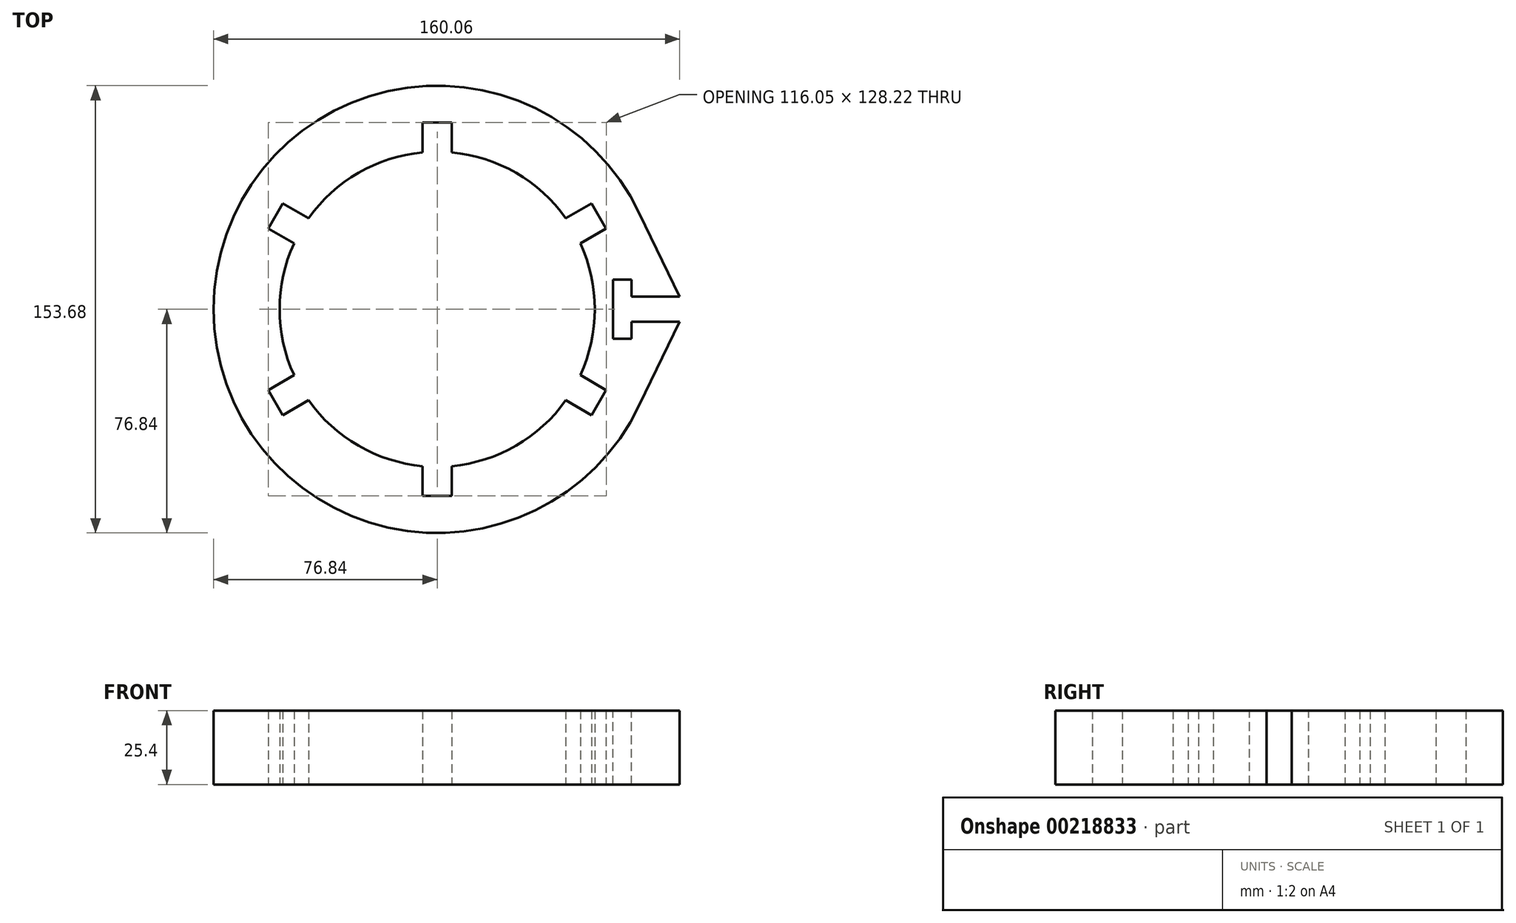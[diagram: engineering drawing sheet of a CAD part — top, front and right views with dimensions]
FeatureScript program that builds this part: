
annotation { "Feature Type Name" : "Feature", "Feature Type Description" : "" }
export const myFeature = defineFeature(function(context is Context, id is Id, definition is map)
    precondition{}
    {
        {
            var Q0;
            Q0=qCreatedBy(makeId("Top.planeOp"),FACE);
            var sketch = newSketch(context, id + "F0", { "sketchPlane" : qUnion([Q0])});
            skCircle(sketch, "E0", {"center": v(0, 0) * mm, "radius": 54.11 * mm});
            skLineSegment(sketch, "E1.bottom", {"start": v(5, 64.11) * mm, "end": v(-5, 64.11) * mm});
            skLineSegment(sketch, "E1.top", {"start": v(5, 44.11) * mm, "end": v(-5, 44.11) * mm});
            skLineSegment(sketch, "E1.left", {"start": v(5, 64.11) * mm, "end": v(5, 44.11) * mm});
            skLineSegment(sketch, "E1.right", {"start": v(-5, 64.11) * mm, "end": v(-5, 44.11) * mm});
            skPoint(sketch, "E1.middle", {"position": v(0, 54.11) * mm});
            skLineSegment(sketch, "E2.1.0", {"start": v(-58.02, 27.73) * mm, "end": v(-40.7, 17.73) * mm});
            skLineSegment(sketch, "E2.1.1", {"start": v(-53.02, 36.39) * mm, "end": v(-58.02, 27.73) * mm});
            skLineSegment(sketch, "E2.1.2", {"start": v(-35.7, 26.39) * mm, "end": v(-40.7, 17.73) * mm});
            skLineSegment(sketch, "E2.1.3", {"start": v(-53.02, 36.39) * mm, "end": v(-35.7, 26.39) * mm});
            skLineSegment(sketch, "E2.2.0", {"start": v(-53.02, -36.39) * mm, "end": v(-35.7, -26.39) * mm});
            skLineSegment(sketch, "E2.2.1", {"start": v(-58.02, -27.73) * mm, "end": v(-53.02, -36.39) * mm});
            skLineSegment(sketch, "E2.2.2", {"start": v(-40.7, -17.73) * mm, "end": v(-35.7, -26.39) * mm});
            skLineSegment(sketch, "E2.2.3", {"start": v(-58.02, -27.73) * mm, "end": v(-40.7, -17.73) * mm});
            skLineSegment(sketch, "E2.3.0", {"start": v(5, -64.11) * mm, "end": v(5, -44.11) * mm});
            skLineSegment(sketch, "E2.3.1", {"start": v(-5, -64.11) * mm, "end": v(5, -64.11) * mm});
            skLineSegment(sketch, "E2.3.2", {"start": v(-5, -44.11) * mm, "end": v(5, -44.11) * mm});
            skLineSegment(sketch, "E2.3.3", {"start": v(-5, -64.11) * mm, "end": v(-5, -44.11) * mm});
            skLineSegment(sketch, "E2.4.0", {"start": v(58.02, -27.73) * mm, "end": v(40.7, -17.73) * mm});
            skLineSegment(sketch, "E2.4.1", {"start": v(53.02, -36.39) * mm, "end": v(58.02, -27.73) * mm});
            skLineSegment(sketch, "E2.4.2", {"start": v(35.7, -26.39) * mm, "end": v(40.7, -17.73) * mm});
            skLineSegment(sketch, "E2.4.3", {"start": v(53.02, -36.39) * mm, "end": v(35.7, -26.39) * mm});
            skLineSegment(sketch, "E2.5.0", {"start": v(53.02, 36.39) * mm, "end": v(35.7, 26.39) * mm});
            skLineSegment(sketch, "E2.5.1", {"start": v(58.02, 27.73) * mm, "end": v(53.02, 36.39) * mm});
            skLineSegment(sketch, "E2.5.2", {"start": v(40.7, 17.73) * mm, "end": v(35.7, 26.39) * mm});
            skLineSegment(sketch, "E2.5.3", {"start": v(58.02, 27.73) * mm, "end": v(40.7, 17.73) * mm});
            skLineSegment(sketch, "E2.anchor1", {"start": v(0, 0) * mm, "end": v(5, 44.11) * mm, "construction": true});
            skLineSegment(sketch, "E2.anchor2", {"start": v(0, 0) * mm, "end": v(5, 44.11) * mm, "construction": true});
            skCircle(sketch, "E3", {"center": v(0, 0) * mm, "radius": 76.84 * mm});
            skSolve(sketch);
        }
        {
            var Q0;
            {var subQ19=sQuery(id+"F0.wireOp",EDGE,"E2.1.1");Q0=makeQuery(id+"F0.imprint","IMPRINT",FACE,{"disambiguationData":[TD([[makeQuery(id+"F0.imprint","IMPRINT",EDGE,{"derivedFrom":subQ19}),-1.0]])]});}
            extrude(context, id + "F1", {"entities" : qUnion([Q0]), "depth" : 25.4 * mm});
        }
        {
            var Q0;
            Q0=makeQuery(id+"F1.opExtrude","CAP_FACE",FACE,{"disambiguationData":[OSD([sQuery(id+"F0.wireOp",EDGE,"E0"),sQuery(id+"F0.wireOp",EDGE,"E2.1.0"),sQuery(id+"F0.wireOp",EDGE,"E2.1.1"),sQuery(id+"F0.wireOp",EDGE,"E2.1.3"),sQuery(id+"F0.wireOp",EDGE,"E2.2.0"),sQuery(id+"F0.wireOp",EDGE,"E2.2.1"),sQuery(id+"F0.wireOp",EDGE,"E2.2.3"),sQuery(id+"F0.wireOp",EDGE,"E2.3.0"),sQuery(id+"F0.wireOp",EDGE,"E2.3.1"),sQuery(id+"F0.wireOp",EDGE,"E2.3.3"),sQuery(id+"F0.wireOp",EDGE,"E2.4.0"),sQuery(id+"F0.wireOp",EDGE,"E2.4.1"),sQuery(id+"F0.wireOp",EDGE,"E2.4.3"),sQuery(id+"F0.wireOp",EDGE,"E2.5.0"),sQuery(id+"F0.wireOp",EDGE,"E2.5.1"),sQuery(id+"F0.wireOp",EDGE,"E2.5.3"),sQuery(id+"F0.wireOp",EDGE,"E3"),sQuery(id+"F0.wireOp",EDGE,"E1.bottom"),sQuery(id+"F0.wireOp",EDGE,"E1.right"),sQuery(id+"F0.wireOp",EDGE,"E1.left")])],"isStart":false});
            var sketch = newSketch(context, id + "F2", { "sketchPlane" : qUnion([Q0])});
            skLineSegment(sketch, "E4", {"start": v(76.16, -10.19) * mm, "end": v(71.64, -4.32) * mm});
            skLineSegment(sketch, "E5", {"start": v(71.64, -4.32) * mm, "end": v(66.68, -4.32) * mm});
            skLineSegment(sketch, "E6", {"start": v(66.68, -4.32) * mm, "end": v(66.68, -10.16) * mm});
            skLineSegment(sketch, "E7", {"start": v(66.68, -10.16) * mm, "end": v(60.33, -10.16) * mm});
            skLineSegment(sketch, "E8", {"start": v(60.33, -10.16) * mm, "end": v(60.33, 0) * mm});
            skPoint(sketch, "E8.endSnap0", {"position": v(54.11, 0) * mm});
            skLineSegment(sketch, "E9", {"start": v(54.11, 0) * mm, "end": v(76.84, 0) * mm});
            skLineSegment(sketch, "E10.MirrorCS", {"start": v(60.33, 10.16) * mm, "end": v(60.33, 0) * mm});
            skLineSegment(sketch, "E11.MirrorCS", {"start": v(66.68, 10.16) * mm, "end": v(60.33, 10.16) * mm});
            skLineSegment(sketch, "E12.MirrorCS", {"start": v(66.68, 4.32) * mm, "end": v(66.68, 10.16) * mm});
            skLineSegment(sketch, "E13.MirrorCS", {"start": v(71.64, 4.32) * mm, "end": v(66.68, 4.32) * mm});
            skLineSegment(sketch, "E14.MirrorCS", {"start": v(76.16, 10.19) * mm, "end": v(71.64, 4.32) * mm});
            skLineSegment(sketch, "E15", {"start": v(71.64, -4.32) * mm, "end": v(76.84, -4.32) * mm});
            skLineSegment(sketch, "E16", {"start": v(71.64, 4.32) * mm, "end": v(76.72, 4.32) * mm});
            skFitSpline(sketch, "E17", {"points": [v(69.43, -32.92) * mm, v(79, -10.72) * mm, v(85.43, -6.68) * mm], "startDerivative": vector(14, 42.13) * mm, "endDerivative": vector(18.45, 7.04) * mm});
            skLineSegment(sketch, "E18", {"start": v(85.43, -6.68) * mm, "end": v(83.22, -4.32) * mm});
            skLineSegment(sketch, "E19", {"start": v(83.22, -4.32) * mm, "end": v(76.84, -4.32) * mm});
            skFitSpline(sketch, "E20.MirrorCS", {"points": [v(69.43, 32.92) * mm, v(79, 10.72) * mm, v(85.43, 6.68) * mm], "startDerivative": vector(14, -42.13) * mm, "endDerivative": vector(18.45, -7.04) * mm});
            skLineSegment(sketch, "E21.MirrorCS", {"start": v(83.22, 4.32) * mm, "end": v(76.84, 4.32) * mm});
            skLineSegment(sketch, "E22.MirrorCS", {"start": v(85.43, 6.68) * mm, "end": v(83.22, 4.32) * mm});
            skLineSegment(sketch, "E23", {"start": v(76.16, -10.19) * mm, "end": v(79, -10.72) * mm});
            skLineSegment(sketch, "E24", {"start": v(76.16, 10.19) * mm, "end": v(79, 10.72) * mm});
            skLineSegment(sketch, "E25", {"start": v(79, 10.72) * mm, "end": v(83.22, 4.32) * mm});
            skLineSegment(sketch, "E26", {"start": v(76.16, 10.19) * mm, "end": v(76.72, 4.32) * mm});
            skLineSegment(sketch, "E27", {"start": v(69.43, -32.92) * mm, "end": v(83.22, -4.32) * mm});
            skLineSegment(sketch, "E28", {"start": v(69.43, 32.92) * mm, "end": v(83.22, 4.32) * mm});
            skLineSegment(sketch, "E29", {"start": v(76.84, 4.32) * mm, "end": v(76.72, 4.32) * mm});
            skSolve(sketch);
        }
        {
            var Q0;
            {var subQ0=sQuery(id+"F2.wireOp",EDGE,"E10.MirrorCS");Q0=makeQuery(id+"F2.imprint","IMPRINT",FACE,{"disambiguationData":[TD([[makeQuery(id+"F2.imprint","IMPRINT",EDGE,{"derivedFrom":subQ0}),1.0]])]});}
            var Q1;
            {var subQ1=sQuery(id+"F2.wireOp",EDGE,"E5");Q1=makeQuery(id+"F2.imprint","IMPRINT",FACE,{"disambiguationData":[TD([[makeQuery(id+"F2.imprint","IMPRINT",EDGE,{"derivedFrom":subQ1}),-1.0]])]});}
            extrude(context, id + "F3", {"entities" : qUnion([Q0, Q1]), "operationType" : NewBodyOperationType.REMOVE, "oppositeDirection" : true, "depth" : 2540 * mm});
        }
        {
            var Q0;
            {var subQ0=sQuery(id+"F2.wireOp",EDGE,"E20.MirrorCS");var subQ2=makeQuery(id+"F1.opExtrude","CAP_EDGE",EDGE,{"disambiguationData":[OSD([sQuery(id+"F0.wireOp",EDGE,"E3")])],"isStart":false});var subQ3=makeQuery(id+"F2.imprint","INTERSECT",VERTEX,{"derivedFrom":[subQ2,subQ0]});Q0=makeQuery(id+"F2.imprint","IMPRINT",FACE,{"disambiguationData":[TD([[makeQuery(id+"F2.imprint","IMPRINT",EDGE,{"disambiguationData":[TD([[subQ3,-1.0]])],"derivedFrom":subQ0}),1.0]])]});}
            var Q1;
            {var subQ0=sQuery(id+"F2.wireOp",EDGE,"E24");Q1=makeQuery(id+"F2.imprint","IMPRINT",FACE,{"disambiguationData":[TD([[makeQuery(id+"F2.imprint","IMPRINT",EDGE,{"derivedFrom":subQ0}),1.0]])]});}
            var Q2;
            Q2=makeQuery(id+"F2.imprint","IMPRINT",FACE,{"disambiguationData":[TD([[makeQuery(id+"F2.imprint","IMPRINT",EDGE,{"derivedFrom":sQuery(id+"F2.wireOp",EDGE,"E21.MirrorCS")}),-1.0]])]});
            var Q3;
            {var subQ0=sQuery(id+"F2.wireOp",EDGE,"E25");Q3=makeQuery(id+"F2.imprint","IMPRINT",FACE,{"disambiguationData":[TD([[makeQuery(id+"F2.imprint","IMPRINT",EDGE,{"derivedFrom":subQ0}),1.0]])]});}
            var Q4;
            {var subQ0=sQuery(id+"F2.wireOp",EDGE,"E19");Q4=makeQuery(id+"F2.imprint","IMPRINT",FACE,{"disambiguationData":[TD([[makeQuery(id+"F2.imprint","IMPRINT",EDGE,{"derivedFrom":subQ0}),1.0]])]});}
            var Q5;
            {var subQ0=sQuery(id+"F2.wireOp",EDGE,"E17");var subQ1=makeQuery(id+"F2.imprint","INTERSECT",VERTEX,{"derivedFrom":[subQ0,sQuery(id+"F2.wireOp",EDGE,"E23")]});Q5=makeQuery(id+"F2.imprint","IMPRINT",FACE,{"disambiguationData":[TD([[makeQuery(id+"F2.imprint","IMPRINT",EDGE,{"disambiguationData":[TD([[subQ1,1.0]])],"derivedFrom":subQ0}),-1.0]])]});}
            var Q6;
            {var subQ0=sQuery(id+"F2.wireOp",EDGE,"E23");Q6=makeQuery(id+"F2.imprint","IMPRINT",FACE,{"disambiguationData":[TD([[makeQuery(id+"F2.imprint","IMPRINT",EDGE,{"derivedFrom":subQ0}),-1.0]])]});}
            extrude(context, id + "F4", {"entities" : qUnion([Q0, Q1, Q2, Q3, Q4, Q5, Q6]), "operationType" : NewBodyOperationType.ADD, "oppositeDirection" : true, "depth" : 25.4 * mm});
        }
    });
